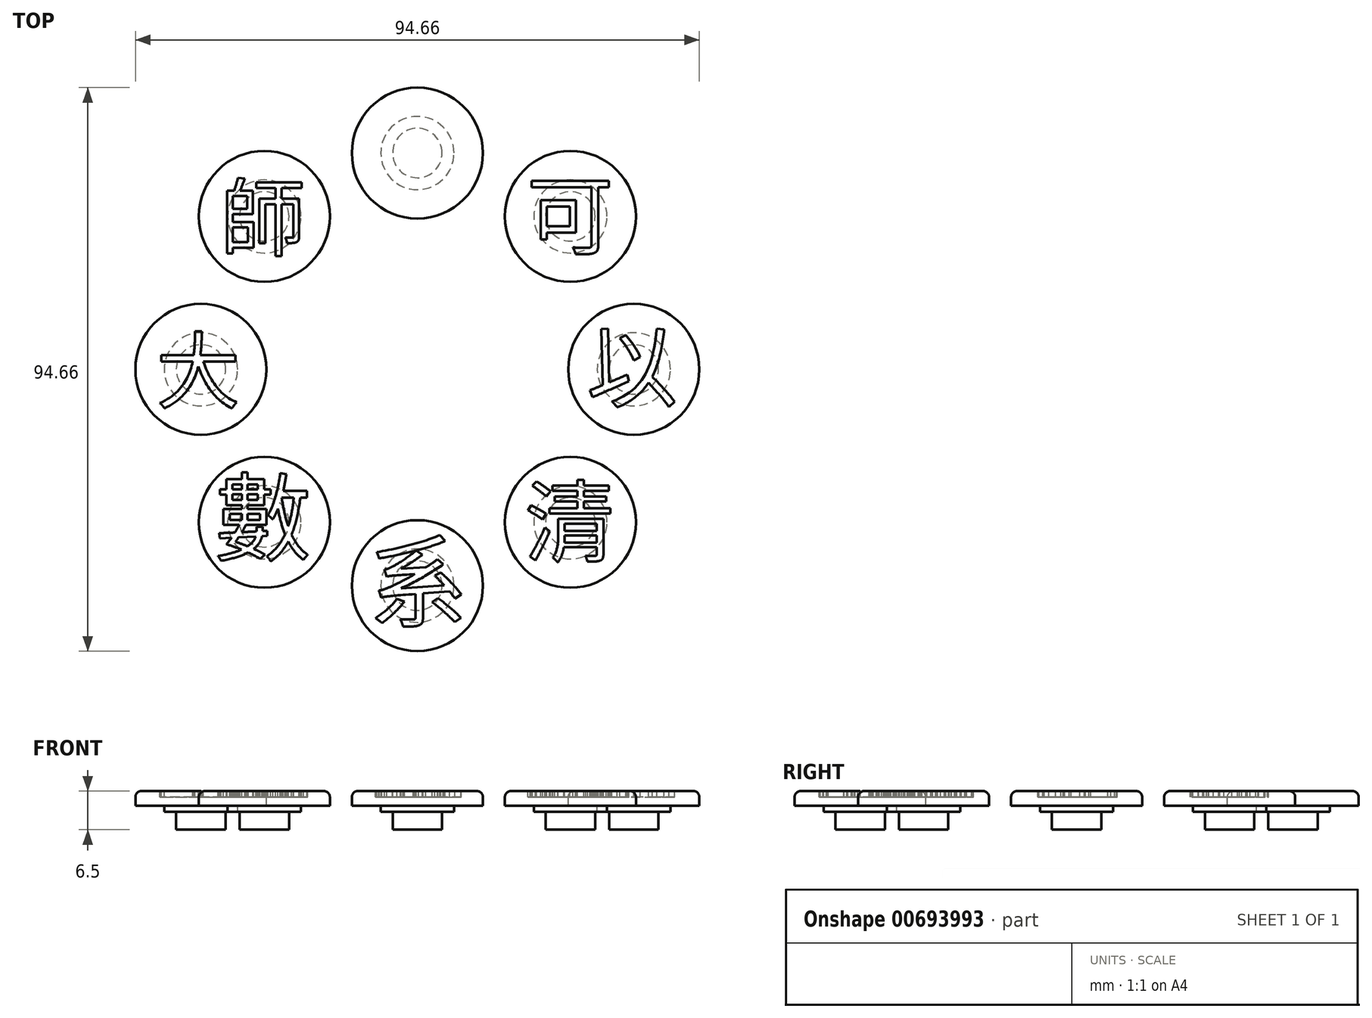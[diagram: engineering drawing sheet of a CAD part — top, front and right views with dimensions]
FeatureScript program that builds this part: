
annotation { "Feature Type Name" : "Feature", "Feature Type Description" : "" }
export const myFeature = defineFeature(function(context is Context, id is Id, definition is map)
    precondition{}
    {
        {
            var Q0;
            Q0=qCreatedBy(makeId("Top.planeOp"),FACE);
            var sketch = newSketch(context, id + "F0", { "sketchPlane" : qUnion([Q0])});
            skCircle(sketch, "E0", {"center": v(0, 0) * mm, "radius": 11 * mm});
            skCircle(sketch, "E1.0", {"center": v(0, 0) * mm, "radius": 4.15 * mm});
            skCircle(sketch, "E2.0", {"center": v(0, 0) * mm, "radius": 6.15 * mm});
            skSolve(sketch);
        }
        {
            var Q0;
            Q0=makeQuery(id+"F0.imprint","IMPRINT",FACE,{"disambiguationData":[TD([[makeQuery(id+"F0.imprint","IMPRINT",EDGE,{"derivedFrom":sQuery(id+"F0.wireOp",EDGE,"E0")}),1.0]])]});
            extrude(context, id + "F1", {"entities" : qUnion([Q0]), "depth" : 2.5 * mm, "offsetDistance" : 25.4 * mm});
        }
        {
            var Q0;
            Q0=makeQuery(id+"F0.imprint","IMPRINT",FACE,{"disambiguationData":[TD([[makeQuery(id+"F0.imprint","IMPRINT",EDGE,{"derivedFrom":sQuery(id+"F0.wireOp",EDGE,"E1.0")}),1.0]])]});
            var Q1;
            Q1=makeQuery(id+"F0.imprint","IMPRINT",FACE,{"disambiguationData":[TD([[makeQuery(id+"F0.imprint","IMPRINT",EDGE,{"derivedFrom":sQuery(id+"F0.wireOp",EDGE,"E1.0")}),-1.0]])]});
            extrude(context, id + "F2", {"entities" : qUnion([Q0, Q1]), "operationType" : NewBodyOperationType.ADD, "depth" : 3.5 * mm, "offsetDistance" : 25.4 * mm});
        }
        {
            var Q0;
            Q0=makeQuery(id+"F0.imprint","IMPRINT",FACE,{"disambiguationData":[TD([[makeQuery(id+"F0.imprint","IMPRINT",EDGE,{"derivedFrom":sQuery(id+"F0.wireOp",EDGE,"E1.0")}),1.0]])]});
            extrude(context, id + "F3", {"entities" : qUnion([Q0]), "operationType" : NewBodyOperationType.ADD, "depth" : 6.5 * mm, "offsetDistance" : 25.4 * mm});
        }
        {
            var Q0;
            Q0=makeQuery(id+"F1.opExtrude","CAP_EDGE",EDGE,{"disambiguationData":[OSD([sQuery(id+"F0.wireOp",EDGE,"E0")])],"isStart":true});
            fillet(context, id + "F4", {"entities" : qUnion([Q0]), "radius" : 1.02 * mm, "tangentPropagation" : true, "allowEdgeOverflow" : false});
        }
        {
            var Q0;
            Q0=qCreatedBy(makeId("Right.planeOp"),FACE);
            var sketch = newSketch(context, id + "F5", { "sketchPlane" : qUnion([Q0])});
            skLineSegment(sketch, "E3", {"start": v(-36.33, -6.15) * mm, "end": v(-36.33, 36.38) * mm});
            skLineSegment(sketch, "E4", {"start": v(0, 0) * mm, "end": v(-88.4, 0) * mm});
            skSolve(sketch);
        }
        {
            var Q0;
            Q0=makeQuery(id+"F1.opExtrude","SWEPT_BODY",BODY,{"disambiguationData":[OSD([sQuery(id+"F0.wireOp",EDGE,"E0"),sQuery(id+"F0.wireOp",EDGE,"E2.0")])]});
            var Q1;
            Q1=sQuery(id+"F5.wireOp",EDGE,"E3");
            circularPattern(context, id + "F6", {"entities" : qUnion([Q0]), "axis" : qUnion([Q1]), "angle" : 360 * degree, "instanceCount" : 8, "equalSpace" : true});
        }
        {
            var Q0;
            Q0=makeQuery(id+"F6.opPattern","COPY",BODY,{"derivedFrom":makeQuery(id+"F1.opExtrude","SWEPT_BODY",BODY,{"disambiguationData":[OSD([sQuery(id+"F0.wireOp",EDGE,"E0"),sQuery(id+"F0.wireOp",EDGE,"E2.0")])]}),"instanceName":"7"});
            var Q1;
            Q1=makeQuery(id+"F1.opExtrude","SWEPT_BODY",BODY,{"disambiguationData":[OSD([sQuery(id+"F0.wireOp",EDGE,"E0"),sQuery(id+"F0.wireOp",EDGE,"E2.0")])]});
            var Q2;
            Q2=makeQuery(id+"F6.opPattern","COPY",BODY,{"derivedFrom":makeQuery(id+"F1.opExtrude","SWEPT_BODY",BODY,{"disambiguationData":[OSD([sQuery(id+"F0.wireOp",EDGE,"E0"),sQuery(id+"F0.wireOp",EDGE,"E2.0")])]}),"instanceName":"1"});
            var Q3;
            Q3=makeQuery(id+"F6.opPattern","COPY",BODY,{"derivedFrom":makeQuery(id+"F1.opExtrude","SWEPT_BODY",BODY,{"disambiguationData":[OSD([sQuery(id+"F0.wireOp",EDGE,"E0"),sQuery(id+"F0.wireOp",EDGE,"E2.0")])]}),"instanceName":"2"});
            var Q4;
            Q4=makeQuery(id+"F6.opPattern","COPY",BODY,{"derivedFrom":makeQuery(id+"F1.opExtrude","SWEPT_BODY",BODY,{"disambiguationData":[OSD([sQuery(id+"F0.wireOp",EDGE,"E0"),sQuery(id+"F0.wireOp",EDGE,"E2.0")])]}),"instanceName":"3"});
            var Q5;
            Q5=makeQuery(id+"F6.opPattern","COPY",BODY,{"derivedFrom":makeQuery(id+"F1.opExtrude","SWEPT_BODY",BODY,{"disambiguationData":[OSD([sQuery(id+"F0.wireOp",EDGE,"E0"),sQuery(id+"F0.wireOp",EDGE,"E2.0")])]}),"instanceName":"4"});
            var Q6;
            Q6=makeQuery(id+"F6.opPattern","COPY",BODY,{"derivedFrom":makeQuery(id+"F1.opExtrude","SWEPT_BODY",BODY,{"disambiguationData":[OSD([sQuery(id+"F0.wireOp",EDGE,"E0"),sQuery(id+"F0.wireOp",EDGE,"E2.0")])]}),"instanceName":"5"});
            var Q7;
            Q7=makeQuery(id+"F6.opPattern","COPY",BODY,{"derivedFrom":makeQuery(id+"F1.opExtrude","SWEPT_BODY",BODY,{"disambiguationData":[OSD([sQuery(id+"F0.wireOp",EDGE,"E0"),sQuery(id+"F0.wireOp",EDGE,"E2.0")])]}),"instanceName":"6"});
            var Q8;
            Q8=sQuery(id+"F5.wireOp",EDGE,"E4");
            transform(context, id + "F7", {"entities" : qUnion([Q0, Q1, Q2, Q3, Q4, Q5, Q6, Q7]), "transformType" : TransformType.ROTATION, "transformAxis" : qUnion([Q8]), "angle" : 180 * degree, "makeCopy" : false});
        }
        {
            var Q0;
            Q0=qCreatedBy(makeId("Top.planeOp"),FACE);
            var sketch = newSketch(context, id + "F8", { "sketchPlane" : qUnion([Q0])});
            skText(sketch, "E5", { "text": "可", "fontName": "NotoSansCJKtc-Regular.otf"});
            skText(sketch, "E6", { "text": "以", "fontName": "NotoSansCJKtc-Regular.otf"});
            skText(sketch, "E7", { "text": "清", "fontName": "NotoSansCJKtc-Regular.otf"});
            skText(sketch, "E8", { "text": "系", "fontName": "NotoSansCJKtc-Regular.otf"});
            skText(sketch, "E9", { "text": "數", "fontName": "NotoSansCJKtc-Regular.otf"});
            skText(sketch, "E10", { "text": "師", "fontName": "NotoSansCJKtc-Regular.otf"});
            skText(sketch, "E11", { "text": "大", "fontName": "NotoSansCJKtc-Regular.otf"});
            const initialGuessF8  = {"E5": [0.01833, -0.01592, 1, 0, 0.01055], "E6": [0.02839, -0.04151, 1, 0, 0.01101], "E7": [0.01798, -0.06751, 1, 0, 0.01086], "E8": [-0.00833, -0.07832, 1, 0, 0.0122], "E9": [-0.03402, -0.06728, 1, 0, 0.01172], "E10": [-0.03315, -0.0162, 1, 0, 0.01038], "E11": [-0.0439, -0.0418, 1, 0, 0.01024]};
            skSetInitialGuess(sketch, initialGuessF8);
            skSolve(sketch);
        }
        {
            var Q0;
            Q0 = qSketchRegion(id + "F8", true);
            extrude(context, id + "F9", {"entities" : qUnion([Q0]), "operationType" : NewBodyOperationType.REMOVE, "oppositeDirection" : true, "depth" : 1 * mm, "offsetDistance" : 25 * mm});
        }
    });
